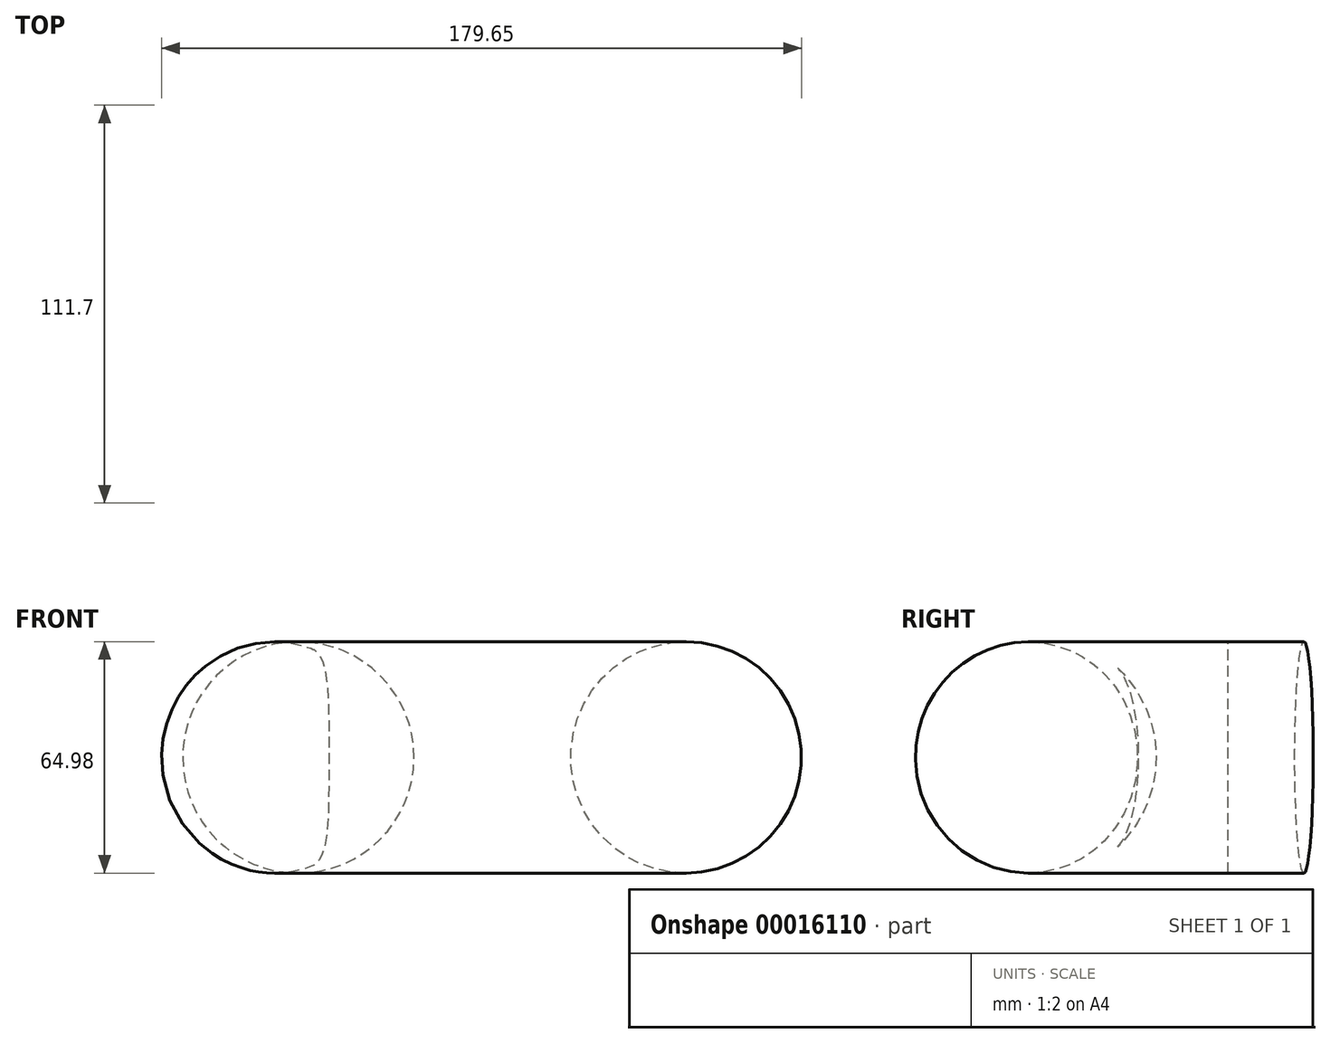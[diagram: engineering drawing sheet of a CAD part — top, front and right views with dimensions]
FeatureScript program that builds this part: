
annotation { "Feature Type Name" : "Feature", "Feature Type Description" : "" }
export const myFeature = defineFeature(function(context is Context, id is Id, definition is map)
    precondition{}
    {
        {
            var Q0;
            Q0=qCreatedBy(makeId("Front.planeOp"),FACE);
            var sketch = newSketch(context, id + "F0", { "sketchPlane" : qUnion([Q0])});
            skCircle(sketch, "E0", {"center": v(0, 0) * mm, "radius": 32.49 * mm});
            skSolve(sketch);
        }
        {
            var Q0;
            Q0=qCreatedBy(makeId("Top.planeOp"),FACE);
            var sketch = newSketch(context, id + "F1", { "sketchPlane" : qUnion([Q0])});
            skFitSpline(sketch, "E1", {"points": [v(0, 0) * mm, v(0, -50.18) * mm, v(79.05, -39.36) * mm, v(108.9, 21.32) * mm], "startDerivative": vector(-59, -210.38) * mm, "endDerivative": vector(39.82, 203) * mm});
            skSolve(sketch);
        }
        {
            var Q0;
            Q0=makeQuery(id+"F0.imprint","IMPRINT",FACE,{"disambiguationData":[TD([[makeQuery(id+"F0.imprint","IMPRINT",EDGE,{"derivedFrom":sQuery(id+"F0.wireOp",EDGE,"E0")}),1.0]])]});
            var Q1;
            Q1=sQuery(id+"F1.wireOp",EDGE,"a96aab67-6cd5-47a7-a3fd-95f8ba23b4a7");
            var Q2;
            Q2=sQuery(id+"F1.wireOp",EDGE,"E1");
            sweep(context, id + "F2", {"profiles" : qUnion([Q0]), "path" : qUnion([Q1, Q2])});
        }
    });
